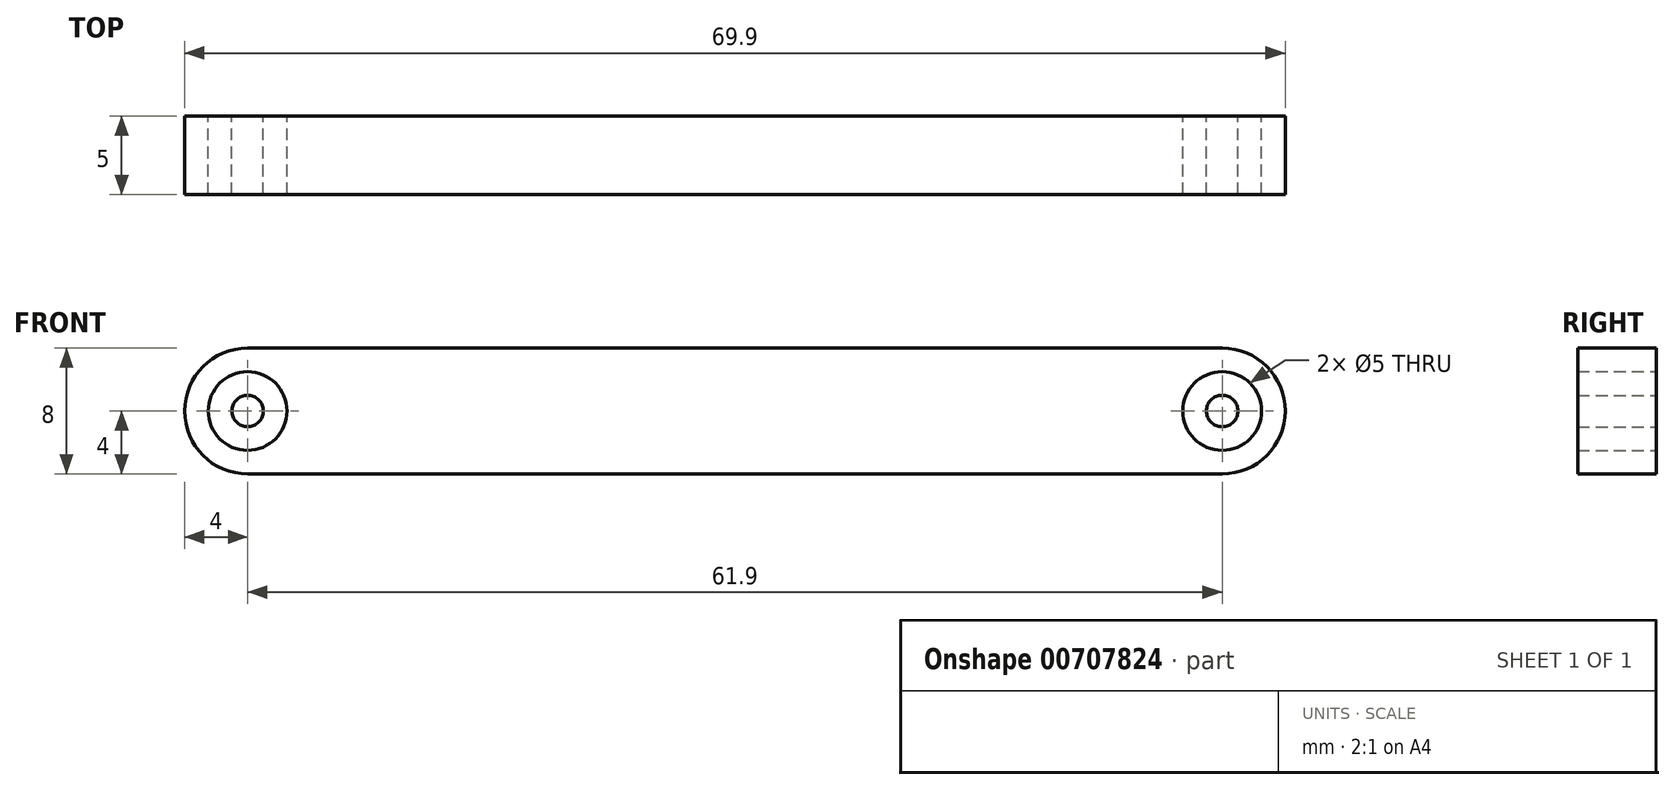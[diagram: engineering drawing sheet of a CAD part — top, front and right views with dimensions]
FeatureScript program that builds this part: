
annotation { "Feature Type Name" : "Feature", "Feature Type Description" : "" }
export const myFeature = defineFeature(function(context is Context, id is Id, definition is map)
    precondition{}
    {
        {
            var Q0;
            Q0=qCreatedBy(makeId("Front.planeOp"),FACE);
            var sketch = newSketch(context, id + "F0", { "sketchPlane" : qUnion([Q0])});
            skArc(sketch, "E0", {"start": v(0, 4) * mm, "mid": v(-4, 0) * mm, "end": v(0, -4) * mm});
            skCircle(sketch, "E1", {"center": v(0, 0) * mm, "radius": 1 * mm});
            skCircle(sketch, "E2", {"center": v(0, 0) * mm, "radius": 2.5 * mm});
            skLineSegment(sketch, "E3", {"start": v(0, 0) * mm, "end": v(61.9, 0) * mm});
            skCircle(sketch, "E4", {"center": v(61.9, 0) * mm, "radius": 2.5 * mm});
            skCircle(sketch, "E5", {"center": v(61.9, 0) * mm, "radius": 1 * mm});
            skArc(sketch, "E6", {"start": v(61.9, -4) * mm, "mid": v(65.9, 0) * mm, "end": v(61.9, 4) * mm});
            skLineSegment(sketch, "E7", {"start": v(0, -4) * mm, "end": v(61.9, -4) * mm});
            skLineSegment(sketch, "E8", {"start": v(0, 4) * mm, "end": v(61.9, 4) * mm});
            skSolve(sketch);
        }
        {
            var Q0;
            Q0=makeQuery(id+"F0.imprint","IMPRINT",FACE,{"disambiguationData":[TD([[makeQuery(id+"F0.imprint","IMPRINT",EDGE,{"derivedFrom":sQuery(id+"F0.wireOp",EDGE,"E0")}),1.0]])]});
            var Q1;
            Q1=makeQuery(id+"F0.imprint","IMPRINT",FACE,{"disambiguationData":[TD([[makeQuery(id+"F0.imprint","IMPRINT",EDGE,{"derivedFrom":sQuery(id+"F0.wireOp",EDGE,"E5")}),1.0]])]});
            var Q2;
            Q2=makeQuery(id+"F0.imprint","IMPRINT",FACE,{"disambiguationData":[TD([[makeQuery(id+"F0.imprint","IMPRINT",EDGE,{"derivedFrom":sQuery(id+"F0.wireOp",EDGE,"E1")}),1.0]])]});
            extrude(context, id + "F1", {"entities" : qUnion([Q0, Q1, Q2]), "depth" : 5 * mm, "offsetDistance" : 25.4 * mm});
        }
    });
